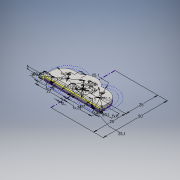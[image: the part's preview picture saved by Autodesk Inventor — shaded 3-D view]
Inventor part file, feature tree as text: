
AUTODESK INVENTOR PART (.ipt)
format: ipt  version: 2016 (Build 200138000, 138)  size: 226,304 bytes
history: native  units: mm
features: extrude x7, other x3, hole x2, sketch x1, projected_geometry x1
ambient origin geometry x8: Origin, YZ Plane, XZ Plane, XY Plane, X Axis, Y Axis, Z Axis, Center Point
bodies: Body1 (feature_tree)
feature tree (14):
  other  "ソリッド1"
  other  "構築線"
  extrude  "外形作成"  Depth=17.0mm
  extrude  "押し出し4"  Depth=5.6mm
  other  "固定具"
  hole  "穴1"  [1 undecoded]
  hole  "穴2"  [1 undecoded]
  extrude  "押し出し5"  Depth=8.6mm
  extrude  "押し出し6"  TaperAngle=0.0deg  [1 undecoded]
  extrude  "押し出し7"  Depth=20.1mm
  extrude  "押し出し8"  TaperAngle=0.0deg  [1 undecoded]
  extrude  "押し出し9"  Depth=25.0mm
  sketch  "スケッチ6"
  projected_geometry  "投影ループ1"
note: 4 required parameter values undecoded (feature->parameter linkage not recoverable at this tier; creation-order binding heuristic only, values carry confidence <= 0.55)
